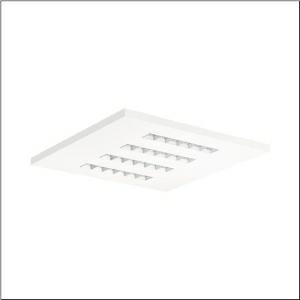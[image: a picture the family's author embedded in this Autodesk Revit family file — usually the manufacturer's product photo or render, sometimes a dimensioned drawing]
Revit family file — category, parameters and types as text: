
# Revit family: silica_21_square_51mx6mtut4w
name_source: partatom
category: Lighting Fixtures
units: mm (PartAtom-declared; Revit-internal decimal feet)

## family parameters
Cut with Voids When Loaded = No
Host = Face
Light Source = No
Part Type = Normal
Room Calculation Point = No
Round Connector Dimension = Use Diameter
Shared = No

## types (1)
- --- (1 x LED 2700 K ... 6500 K, 3720 lm, 30.7 W, 6500K)
    Apparent Load = 31 VA
    CIE Flux Codes = 81 98 100 100 100
    Color Rendering = 80
    Color Temperature = 6500K
    Default Elevation = 1800 mm
    Description = Silica 21 Square, office luminaire, primary light control with lens, of PMMA, primary anti-glare with reflector, of PC, white, CAT 2 (L<= 3000cd/m²), light emission: direct distribution, primary light characteristic: symmetric, installation type: lay-in mounting, LED, rated luminous flux: 3.720lm, luminous efficacy: 113lm/W, light colour: 8tw, colour temperature: 2700..6500K, control gear: DALI-2 DT8, with terminal, 5-pole, mains connection: 220..240V, AC, 50/60Hz, rated input power: 32.8W, luminaire housing, of aluminium, traffic white (RAL 9016), module: M625, length: 622mm, width: 622mm, height: 32mm, protection rating (complete): IP20, insulation class (complete): insulation class I (protective earthing), certification: CE, ENEC, VDE, permissible operating ambient temperature: 0..+35°C, standard: EN 50419, packaging unit: 1 piece
    Height = 0 mm  [stored 0 ft]
    Lamp = 1 x LED 2700 K ... 6500 K
    Lamp Light Flux = 3720 lm
    Lamp Power = 30.7 W
    Lamp count = 1
    Length = 622 mm
    Luminous efficacy = 121 lm/W
    Manufacturer = Siteco
    ModVariant = No
    Model = 51MX6MTUT4W
    Mounting Place = Ceiling
    Mounting Type = Recessed
    Number of Poles = 1
    OnlyDefault = Yes
    Power Factor = 1
    Product Name = Silica 21 Square
    Product group = office luminaire | ceiling recessed
    ProductGroupID = 400
    Protection Class = Protection class I
    Protection Degree = IP 20
    RLX_Detail_Level = 1
    RLX_Emergency_Light_Flux = 0 lm
    RLX_Emergency_Type = 0
    RLX_Emergency_Type_DB = No
    RlxData = <blob elided: 22445 chars, md5=8c33b3c3>
    Socket = socket
    Standby Power = 0 W
    System Light Flux = 3720 lm
    System Power = 31 W
    Type Comments = individual setting: CCT=6500K, colour temperature 6500K, luminous flux: 100 % | dim-lin: 254 | 381 mA
    Type Image = l_1275220.jpg
    URL = http://relux.com
    VarID = @adj_071245
    Voltage = 0 V
    Weight = 0.00 kg
    Width = 622 mm

note: [stored X ft] marks values corroborated as IEEE doubles in the binary element streams (Revit-internal decimal feet)

## geometry (parser evidence)
native form markers: Blend x4, Sweep x12
no freeform markers — native parametric forms only
